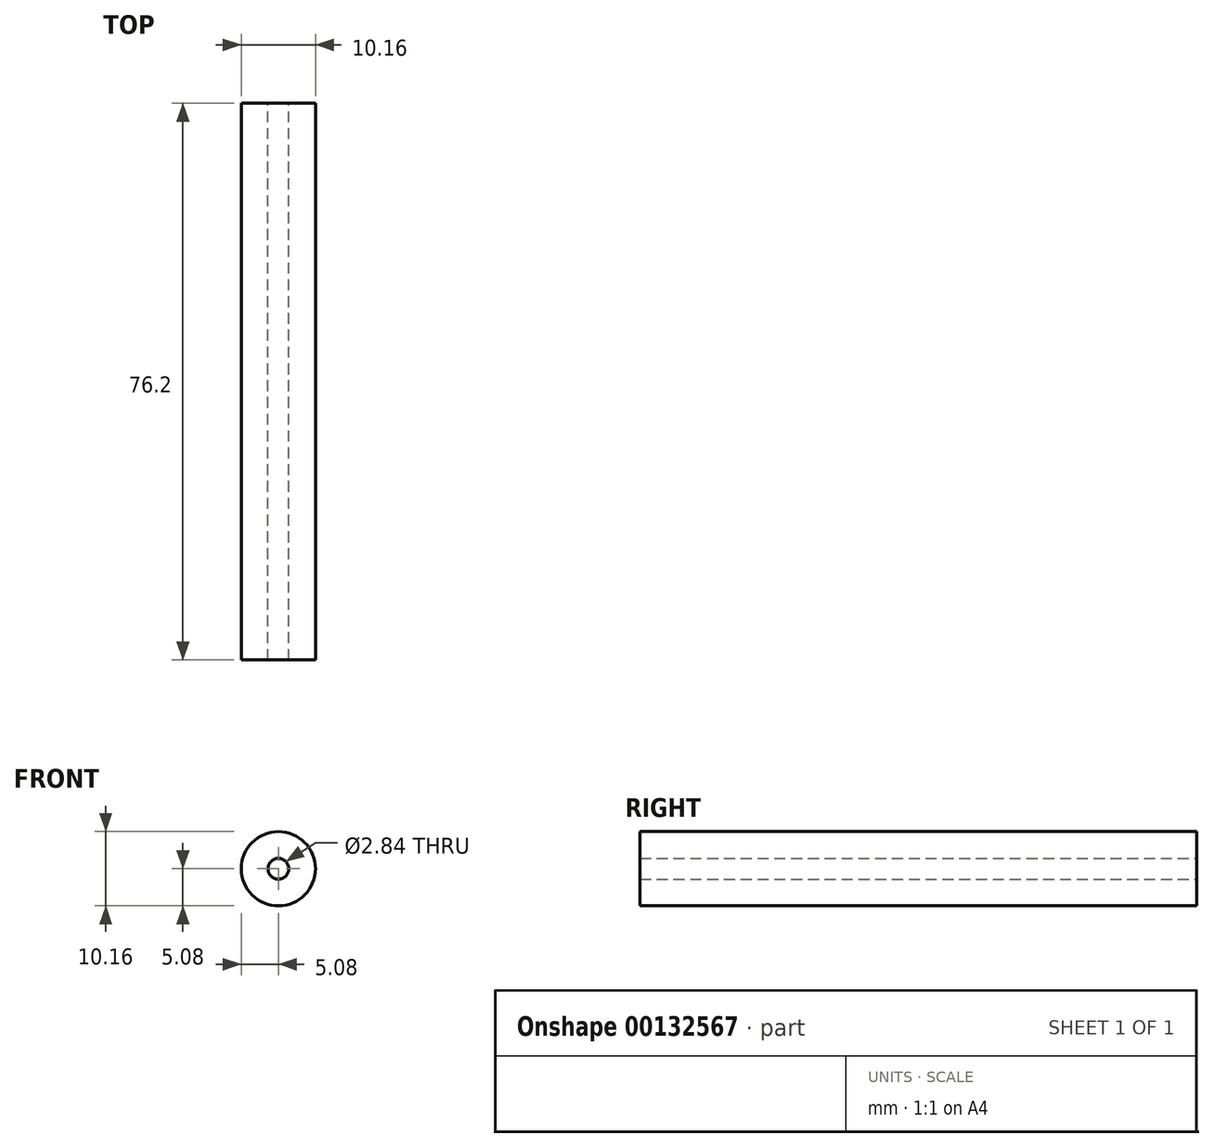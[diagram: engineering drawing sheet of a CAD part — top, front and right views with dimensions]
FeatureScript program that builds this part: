
annotation { "Feature Type Name" : "Feature", "Feature Type Description" : "" }
export const myFeature = defineFeature(function(context is Context, id is Id, definition is map)
    precondition{}
    {
        {
            var Q0;
            Q0=qCreatedBy(makeId("Front.planeOp"),FACE);
            var sketch = newSketch(context, id + "F0", { "sketchPlane" : qUnion([Q0])});
            skCircle(sketch, "E0", {"center": v(0, 0) * mm, "radius": 5.08 * mm});
            skCircle(sketch, "E1", {"center": v(0, 0) * mm, "radius": 1.42 * mm});
            skSolve(sketch);
        }
        {
            var Q0;
            Q0=makeQuery(id+"F0.imprint","IMPRINT",FACE,{"disambiguationData":[TD([[makeQuery(id+"F0.imprint","IMPRINT",EDGE,{"derivedFrom":sQuery(id+"F0.wireOp",EDGE,"E0")}),1.0]])]});
            extrude(context, id + "F1", {"entities" : qUnion([Q0]), "depth" : 76.2 * mm});
        }
    });
